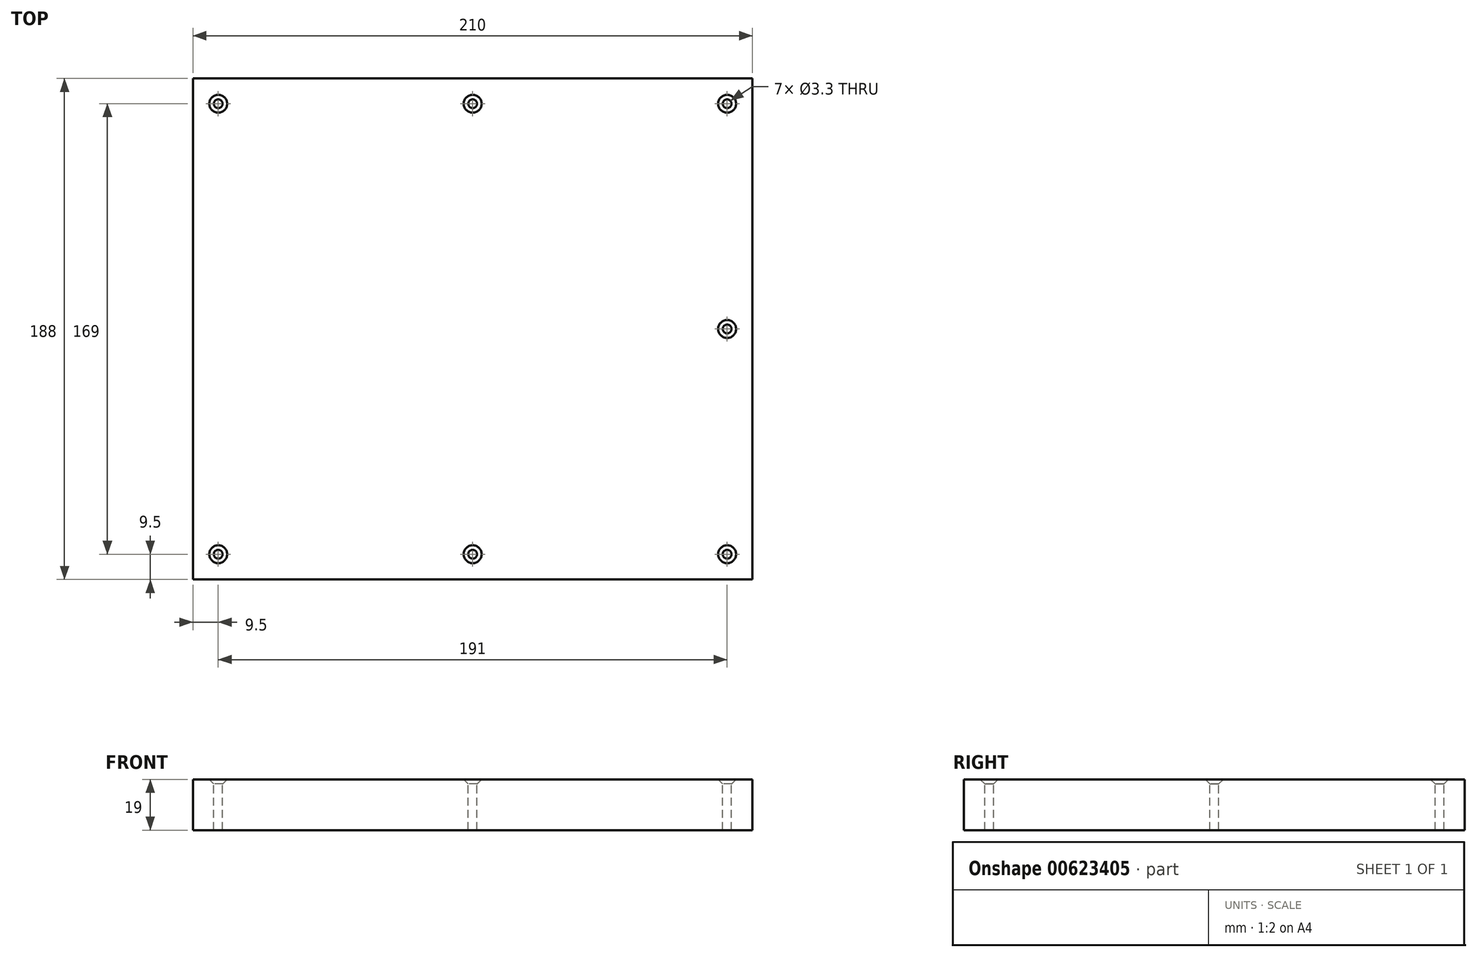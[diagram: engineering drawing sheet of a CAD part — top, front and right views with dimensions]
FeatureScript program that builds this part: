
annotation { "Feature Type Name" : "Feature", "Feature Type Description" : "" }
export const myFeature = defineFeature(function(context is Context, id is Id, definition is map)
    precondition{}
    {
        {
            var Q0;
            Q0=qCreatedBy(makeId("Top.planeOp"),FACE);
            var sketch = newSketch(context, id + "F0", { "sketchPlane" : qUnion([Q0])});
            skLineSegment(sketch, "E0.bottom", {"start": v(105, 94) * mm, "end": v(-105, 94) * mm});
            skLineSegment(sketch, "E0.top", {"start": v(105, -94) * mm, "end": v(-105, -94) * mm});
            skLineSegment(sketch, "E0.left", {"start": v(105, 94) * mm, "end": v(105, -94) * mm});
            skLineSegment(sketch, "E0.right", {"start": v(-105, 94) * mm, "end": v(-105, -94) * mm});
            skPoint(sketch, "E0.middle", {"position": v(0, 0) * mm});
            skSolve(sketch);
        }
        {
            var Q0;
            Q0 = qSketchRegion(id + "F0", true);
            extrude(context, id + "F1", {"entities" : qUnion([Q0]), "depth" : -19 * mm, "offsetDistance" : 25 * mm});
        }
        {
            var Q0;
            Q0=makeQuery(id+"F1.opExtrude","CAP_FACE",FACE,{"disambiguationData":[OSD([sQuery(id+"F0.wireOp",EDGE,"E0.bottom"),sQuery(id+"F0.wireOp",EDGE,"E0.top"),sQuery(id+"F0.wireOp",EDGE,"E0.left"),sQuery(id+"F0.wireOp",EDGE,"E0.right")])],"isStart":true});
            var sketch = newSketch(context, id + "F2", { "sketchPlane" : qUnion([Q0])});
            skPoint(sketch, "E1", {"position": v(-95.5, 84.5) * mm});
            skPoint(sketch, "E2", {"position": v(95.5, 84.5) * mm});
            skPoint(sketch, "E3", {"position": v(95.5, -84.5) * mm});
            skPoint(sketch, "E4", {"position": v(-95.5, -84.5) * mm});
            skPoint(sketch, "E5", {"position": v(0, 84.5) * mm});
            skPoint(sketch, "E6", {"position": v(0, -84.5) * mm});
            skPoint(sketch, "E7", {"position": v(95.5, 0) * mm});
            skSolve(sketch);
        }
        {
            var Q0;
            Q0=sQuery(id+"F2.wireOp",VERTEX,"E1");
            var Q1;
            Q1=sQuery(id+"F2.wireOp",VERTEX,"E5");
            var Q2;
            Q2=sQuery(id+"F2.wireOp",VERTEX,"E2");
            var Q3;
            Q3=sQuery(id+"F2.wireOp",VERTEX,"E7");
            var Q4;
            Q4=sQuery(id+"F2.wireOp",VERTEX,"E3");
            var Q5;
            Q5=sQuery(id+"F2.wireOp",VERTEX,"E6");
            var Q6;
            Q6=sQuery(id+"F2.wireOp",VERTEX,"E4");
            var Q7;
            Q7=makeQuery(id+"F1.opExtrude","SWEPT_BODY",BODY,{"disambiguationData":[OSD([sQuery(id+"F0.wireOp",EDGE,"E0.bottom"),sQuery(id+"F0.wireOp",EDGE,"E0.top"),sQuery(id+"F0.wireOp",EDGE,"E0.left"),sQuery(id+"F0.wireOp",EDGE,"E0.right")])]});
            hole(context, id + "F3", {"style" : HoleStyle.C_SINK, "endStyle" : HoleEndStyle.THROUGH, "standardTappedOrClearance" : lookupTablePath({ "standard" : "ISO", "fit" : "Normal", "size" : "M3", "type" : "Clearance" }), "standardBlindInLast" : lookupTablePath({ "fit" : "Standard", "standard" : "ISO", "size" : "M3", "type" : "Clearance" }), "holeDiameter" : 3.3 * mm, "cSinkDiameter" : 6.72 * mm, "cSinkAngle" : 90 * degree, "majorDiameter" : 5 * mm, "isTappedThrough" : true, "tappedDepth" : 12 * mm, "tapClearance" : 3, "startFromSketch" : true, "locations" : qUnion([Q0, Q1, Q2, Q3, Q4, Q5, Q6]), "scope" : qUnion([Q7])});
        }
    });
